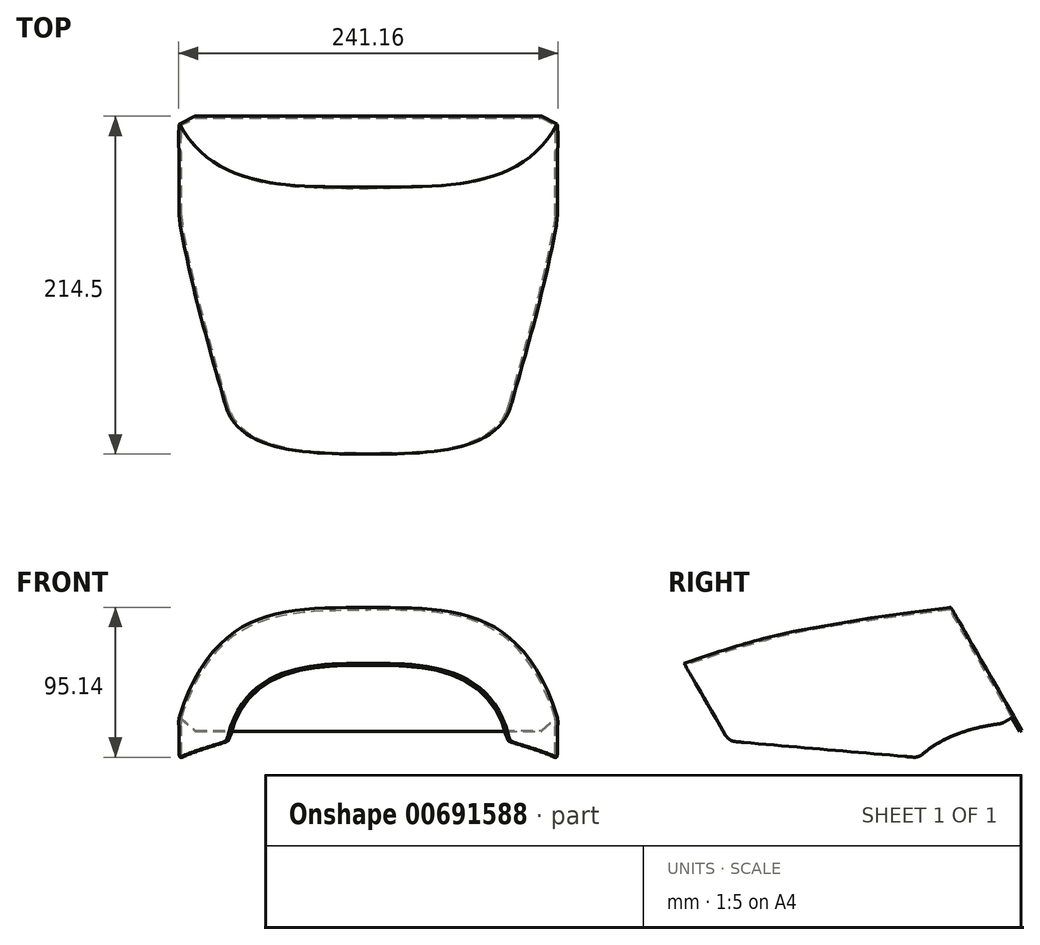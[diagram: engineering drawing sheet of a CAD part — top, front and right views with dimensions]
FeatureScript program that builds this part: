
annotation { "Feature Type Name" : "Feature", "Feature Type Description" : "" }
export const myFeature = defineFeature(function(context is Context, id is Id, definition is map)
    precondition{}
    {
        {
            var Q0;
            Q0=qCreatedBy(makeId("Right.planeOp"),FACE);
            var sketch = newSketch(context, id + "F0", { "sketchPlane" : qUnion([Q0])});
            skLineSegment(sketch, "E0", {"start": v(0, 0) * mm, "end": v(-40, 69.28) * mm});
            skLineSegment(sketch, "E1", {"start": v(-181, -15.59) * mm, "end": v(-60.46, -26.13) * mm});
            skLineSegment(sketch, "E2", {"start": v(-181, -15.59) * mm, "end": v(-209.5, 33.77) * mm});
            skFitSpline(sketch, "E3", {"points": [v(-209.5, 33.77) * mm, v(-40, 69.28) * mm], "startDerivative": vector(171.13, 58.84) * mm, "endDerivative": vector(216.69, 23.06) * mm});
            skFitSpline(sketch, "E4", {"points": [v(-60.46, -26.13) * mm, v(-15.76, -6.37) * mm], "startDerivative": vector(39.64, 38.44) * mm, "endDerivative": vector(60.06, 7.2) * mm});
            skLineSegment(sketch, "E5", {"start": v(-15.76, -6.37) * mm, "end": v(0, 0) * mm});
            skLineSegment(sketch, "E6", {"start": v(0, 0) * mm, "end": v(-190, 0) * mm, "construction": true});
            skLineSegment(sketch, "E7", {"start": v(-129.54, 56.19) * mm, "end": v(-60.46, -26.13) * mm, "construction": true});
            skPoint(sketch, "E8", {"position": v(-82.39, 0) * mm});
            skSolve(sketch);
        }
        {
            var Q0;
            Q0=sQuery(id+"F0.wireOp",EDGE,"E2");
            cPlane(context, id + "F1", {"entities" : qUnion([Q0]), "cplaneType" : CPlaneType.LINE_ANGLE, "offset" : 25 * mm, "angle" : 90 * degree, "oppositeDirection" : true, "width" : 150 * mm, "height" : 150 * mm});
        }
        {
            var Q0;
            Q0=sQuery(id+"F0.wireOp",EDGE,"E7");
            cPlane(context, id + "F2", {"entities" : qUnion([Q0]), "cplaneType" : CPlaneType.LINE_ANGLE, "offset" : 25 * mm, "angle" : 90 * degree, "oppositeDirection" : true, "width" : 150 * mm, "height" : 150 * mm});
        }
        {
            var Q0;
            Q0=sQuery(id+"F0.wireOp",EDGE,"E0");
            cPlane(context, id + "F3", {"entities" : qUnion([Q0]), "cplaneType" : CPlaneType.LINE_ANGLE, "offset" : 25 * mm, "angle" : 90 * degree, "oppositeDirection" : true, "width" : 150 * mm, "height" : 150 * mm});
        }
        {
            var Q0;
            Q0=qCreatedBy(id+"F1.planeOp",FACE);
            var sketch = newSketch(context, id + "F4", { "sketchPlane" : qUnion([Q0])});
            skLineSegment(sketch, "E9", {"start": v(90, 77) * mm, "end": v(-90, 77) * mm});
            skLineSegment(sketch, "E10", {"start": v(0, 77) * mm, "end": v(0, 134) * mm, "construction": true});
            skLineSegment(sketch, "E11", {"start": v(-79.13, 134) * mm, "end": v(79.13, 134) * mm, "construction": true});
            skFitSpline(sketch, "E12", {"points": [v(0, 134) * mm, v(90, 77) * mm], "startDerivative": vector(105, 0) * mm, "endDerivative": vector(32.62, -171) * mm});
            skFitSpline(sketch, "E13", {"points": [v(-90, 77) * mm, v(0, 134) * mm], "startDerivative": vector(32.62, 171) * mm, "endDerivative": vector(105, 0) * mm});
            skSolve(sketch);
        }
        {
            var Q0;
            Q0=qCreatedBy(id+"F2.planeOp",FACE);
            var sketch = newSketch(context, id + "F5", { "sketchPlane" : qUnion([Q0])});
            skLineSegment(sketch, "E14", {"start": v(0, 126.3) * mm, "end": v(0, 18.84) * mm, "construction": true});
            skLineSegment(sketch, "E15", {"start": v(-98.28, 126.3) * mm, "end": v(98.28, 126.3) * mm, "construction": true});
            skLineSegment(sketch, "E16", {"start": v(-120, 18.84) * mm, "end": v(120, 18.84) * mm});
            skFitSpline(sketch, "E17", {"points": [v(-120, 18.84) * mm, v(0, 126.3) * mm], "startDerivative": vector(65.17, 322.4) * mm, "endDerivative": vector(120, 0) * mm});
            skFitSpline(sketch, "E18", {"points": [v(0, 126.3) * mm, v(120, 18.84) * mm], "startDerivative": vector(120, 0) * mm, "endDerivative": vector(65.17, -322.4) * mm});
            skLineSegment(sketch, "E19", {"start": v(103.42, 52.96) * mm, "end": v(-103.42, 52.96) * mm, "construction": true});
            skSolve(sketch);
        }
        {
            var Q0;
            Q0=qCreatedBy(id+"F3.planeOp",FACE);
            var sketch = newSketch(context, id + "F6", { "sketchPlane" : qUnion([Q0])});
            skLineSegment(sketch, "E20", {"start": v(0, 0) * mm, "end": v(0, 80) * mm, "construction": true});
            skLineSegment(sketch, "E21", {"start": v(-120, 0) * mm, "end": v(120, 0) * mm});
            skLineSegment(sketch, "E22", {"start": v(-97.82, 80) * mm, "end": v(97.82, 80) * mm, "construction": true});
            skFitSpline(sketch, "E23", {"points": [v(0, 80) * mm, v(120, 0) * mm], "startDerivative": vector(165, 0) * mm, "endDerivative": vector(66.55, -240) * mm});
            skFitSpline(sketch, "E24", {"points": [v(0, 80) * mm, v(-120, 0) * mm], "startDerivative": vector(-165, 0) * mm, "endDerivative": vector(-66.55, -240) * mm});
            skSolve(sketch);
        }
        {
            var Q0;
            Q0=makeQuery(id+"F4.imprint","IMPRINT",FACE,{"disambiguationData":[TD([[makeQuery(id+"F4.imprint","IMPRINT",EDGE,{"derivedFrom":sQuery(id+"F4.wireOp",EDGE,"E9")}),-1.0]])]});
            var Q1;
            Q1=makeQuery(id+"F5.imprint","IMPRINT",FACE,{"disambiguationData":[TD([[makeQuery(id+"F5.imprint","IMPRINT",EDGE,{"derivedFrom":sQuery(id+"F5.wireOp",EDGE,"E16")}),1.0]])]});
            var Q2;
            Q2=makeQuery(id+"F6.imprint","IMPRINT",FACE,{"disambiguationData":[TD([[makeQuery(id+"F6.imprint","IMPRINT",EDGE,{"derivedFrom":sQuery(id+"F6.wireOp",EDGE,"E21")}),1.0]])]});
            loft(context, id + "F7", {"sheetProfilesArray" : [{ "sheetProfileEntities" : qUnion([Q0]) }, { "sheetProfileEntities" : qUnion([Q1]) }, { "sheetProfileEntities" : qUnion([Q2]) }]});
        }
        {
            var Q0;
            Q0=qCreatedBy(makeId("Right.planeOp"),FACE);
            var sketch = newSketch(context, id + "F8", { "sketchPlane" : qUnion([Q0])});
            skLineSegment(sketch, "E25", {"start": v(-181, -15.59) * mm, "end": v(-60.46, -26.13) * mm});
            skFitSpline(sketch, "E26", {"points": [v(-60.46, -26.13) * mm, v(-7.68, -4.43) * mm], "startDerivative": vector(39.64, 38.44) * mm, "endDerivative": vector(60.06, 7.2) * mm});
            skLineSegment(sketch, "E27", {"start": v(-7.68, -4.43) * mm, "end": v(0, 0) * mm});
            skLineSegment(sketch, "E28", {"start": v(-181, -15.59) * mm, "end": v(-209.22, -24.46) * mm});
            skLineSegment(sketch, "E29", {"start": v(-209.22, -24.46) * mm, "end": v(-191.25, -53.17) * mm});
            skLineSegment(sketch, "E30", {"start": v(-191.25, -53.17) * mm, "end": v(39.83, -53.17) * mm});
            skLineSegment(sketch, "E31", {"start": v(39.83, -53.17) * mm, "end": v(39.83, -0.7) * mm});
            skLineSegment(sketch, "E32", {"start": v(39.83, -0.7) * mm, "end": v(0, 0) * mm});
            skLineSegment(sketch, "E33", {"start": v(0, 0) * mm, "end": v(-40, 69.28) * mm, "construction": true});
            skSolve(sketch);
        }
        {
            var Q0;
            Q0=makeQuery(id+"F8.imprint","IMPRINT",FACE,{"disambiguationData":[TD([[makeQuery(id+"F8.imprint","IMPRINT",EDGE,{"derivedFrom":sQuery(id+"F8.wireOp",EDGE,"E25")}),-1.0]])]});
            extrude(context, id + "F9", {"entities" : qUnion([Q0]), "operationType" : NewBodyOperationType.REMOVE, "endBound" : BoundingType.THROUGH_ALL, "oppositeDirection" : true, "depth" : 25 * mm, "offsetDistance" : 25 * mm, "hasSecondDirection" : true, "secondDirectionBound" : SecondDirectionBoundingType.THROUGH_ALL, "secondDirectionOppositeDirection" : false, "secondDirectionDepth" : 25 * mm});
        }
        {
            var Q0;
            {var subQ0=sQuery(id+"F4.wireOp",EDGE,"E9");var subQ1=sQuery(id+"F4.wireOp",EDGE,"E13");var subQ2=sQuery(id+"F4.wireOp",EDGE,"E12");Q0=makeQuery(id+"F9.boolean.opBoolean","MERGE",EDGE,{"derivedFrom":[makeQuery(id+"F7.opLoft","MID_CAP_EDGE",EDGE,{"disambiguationData":[OSD([subQ0,subQ2,subQ1]),TDD([makeQuery(id+"F4.imprint","INTERSECT",VERTEX,{"derivedFrom":[subQ0,subQ2]}),makeQuery(id+"F4.imprint","INTERSECT",VERTEX,{"derivedFrom":[subQ0,subQ1]}),makeQuery(id+"F4.imprint","IMPRINT",EDGE,{"derivedFrom":subQ0})])],"capPos":0.0}),makeQuery(id+"F9.opExtrude","SWEPT_EDGE",EDGE,{"disambiguationData":[OSD([sQuery(id+"F8.wireOp",EDGE,"E25"),sQuery(id+"F8.wireOp",EDGE,"E28")])]})]});}
            var Q1;
            Q1=makeQuery(id+"F9.boolean.opBoolean","COPY",EDGE,{"derivedFrom":makeQuery(id+"F9.opExtrude","SWEPT_EDGE",EDGE,{"disambiguationData":[OSD([sQuery(id+"F8.wireOp",EDGE,"E25"),sQuery(id+"F8.wireOp",EDGE,"E26")])]})});
            var Q2;
            Q2=makeQuery(id+"F9.boolean.opBoolean","COPY",EDGE,{"derivedFrom":makeQuery(id+"F9.opExtrude","SWEPT_EDGE",EDGE,{"disambiguationData":[OSD([sQuery(id+"F8.wireOp",EDGE,"E26"),sQuery(id+"F8.wireOp",EDGE,"E27")])]})});
            fillet(context, id + "F10", {"entities" : qUnion([Q0, Q1, Q2]), "radius" : 8 * mm, "tangentPropagation" : true, "allowEdgeOverflow" : false});
        }
        {
            var Q0;
            Q0=makeQuery(id+"F7.opLoft","CAP_FACE",FACE,{"disambiguationData":[OSD([makeQuery(id+"F4.imprint","IMPRINT",FACE,{"disambiguationData":[TD([[makeQuery(id+"F4.imprint","IMPRINT",EDGE,{"derivedFrom":sQuery(id+"F4.wireOp",EDGE,"E9")}),-1.0]])]})])],"isStart":true});
            var Q1;
            Q1=makeQuery(id+"F10.opFillet","BLEND_FACE",FACE,{"disambiguationData":[OSD([sQuery(id+"F4.wireOp",EDGE,"E9"),sQuery(id+"F4.wireOp",EDGE,"E12"),sQuery(id+"F4.wireOp",EDGE,"E13"),sQuery(id+"F8.wireOp",EDGE,"E25"),sQuery(id+"F8.wireOp",EDGE,"E28")])]});
            var Q2;
            Q2=makeQuery(id+"F9.boolean.opBoolean","COPY",FACE,{"derivedFrom":makeQuery(id+"F9.opExtrude","SWEPT_FACE",FACE,{"disambiguationData":[OSD([sQuery(id+"F8.wireOp",EDGE,"E25")])]})});
            var Q3;
            Q3=makeQuery(id+"F10.opFillet","BLEND_FACE",FACE,{"disambiguationData":[OSD([sQuery(id+"F8.wireOp",EDGE,"E25"),sQuery(id+"F8.wireOp",EDGE,"E26")])]});
            var Q4;
            Q4=makeQuery(id+"F9.boolean.opBoolean","COPY",FACE,{"derivedFrom":makeQuery(id+"F9.opExtrude","SWEPT_FACE",FACE,{"disambiguationData":[OSD([sQuery(id+"F8.wireOp",EDGE,"E26")])]})});
            var Q5;
            Q5=makeQuery(id+"F10.opFillet","BLEND_FACE",FACE,{"disambiguationData":[OSD([sQuery(id+"F8.wireOp",EDGE,"E26"),sQuery(id+"F8.wireOp",EDGE,"E27")])]});
            var Q6;
            Q6=makeQuery(id+"F9.boolean.opBoolean","COPY",FACE,{"derivedFrom":makeQuery(id+"F9.opExtrude","SWEPT_FACE",FACE,{"disambiguationData":[OSD([sQuery(id+"F8.wireOp",EDGE,"E27")])]})});
            shell(context, id + "F11", {"entities" : qUnion([Q0, Q1, Q2, Q3, Q4, Q5, Q6]), "thickness" : 1.5 * mm});
        }
        {
            var Q0;
            Q0=makeQuery(id+"F6.imprint","IMPRINT",FACE,{"disambiguationData":[TD([[makeQuery(id+"F6.imprint","IMPRINT",EDGE,{"derivedFrom":sQuery(id+"F6.wireOp",EDGE,"E21")}),1.0]])]});
            var sketch = newSketch(context, id + "F12", { "sketchPlane" : qUnion([Q0])});
            skLineSegment(sketch, "E34", {"start": v(110, -10) * mm, "end": v(120, 0) * mm});
            skLineSegment(sketch, "E35", {"start": v(-120, 0) * mm, "end": v(-110, -10) * mm});
            skLineSegment(sketch, "E36", {"start": v(-110, -10) * mm, "end": v(110, -10) * mm});
            skLineSegment(sketch, "E37", {"start": v(120, 0) * mm, "end": v(-120, 0) * mm});
            skSolve(sketch);
        }
        {
            var Q0;
            Q0=makeQuery(id+"F12.imprint","IMPRINT",FACE,{"disambiguationData":[TD([[makeQuery(id+"F12.imprint","IMPRINT",EDGE,{"derivedFrom":sQuery(id+"F12.wireOp",EDGE,"E34")}),1.0]])]});
            extrude(context, id + "F13", {"entities" : qUnion([Q0]), "operationType" : NewBodyOperationType.ADD, "depth" : 1.5 * mm, "offsetDistance" : 25 * mm});
        }
    });
